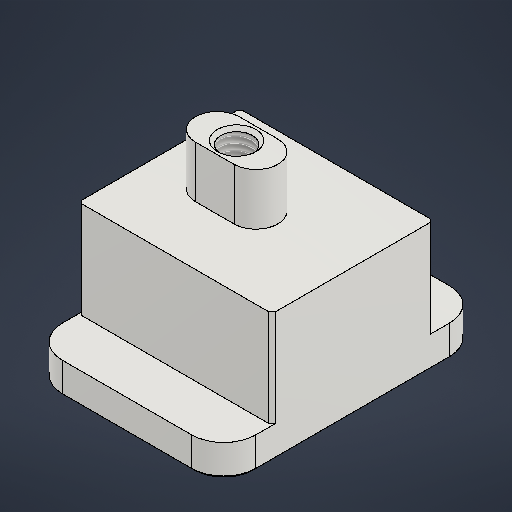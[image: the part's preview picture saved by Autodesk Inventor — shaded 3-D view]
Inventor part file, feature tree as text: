
AUTODESK INVENTOR PART (.ipt)
format: ipt  version: 2025.3 (Build 293356000, 356)  size: 249,344 bytes
history: native  units: mm
features: extrude x4, sketch x2, hole x1, fillet x1, chamfer x1
ambient origin geometry x8: Origin, YZ Plane, XZ Plane, XY Plane, X Axis, Y Axis, Z Axis, Center Point
bodies: Solid1 (feature_tree)
feature tree (9):
  sketch  "Sketch1"  dims[d0=40.0mm d1=30.0mm]
  extrude  "Extrusion1"  Depth=30.0mm
  extrude  "Extrusion2"  Depth=6.8mm
  extrude  "Extrusion5"  Depth=28.0mm
  extrude  "Extrusion6"  TaperAngle=0.0deg  [1 undecoded]
  hole  "Hole1"  [1 undecoded]
  fillet  "Fillet1"  [1 undecoded]
  chamfer  "Chamfer1"  Distance=10.0mm
  sketch  "Sketch3"  dims[d2=6.0mm d3=6.8mm d4=28.0mm d5=0.0mm d6=8.0mm d7=0.0mm d8=4.917mm d9=10.0mm d10=6.0mm d11=2.0mm d12=90.0deg d13=15.0mm d14=0.0mm d15=5.0mm d16=0.5mm d17=2.0mm d18=45.0deg d19=3.0mm d29=15.0mm d30=15.0mm d31=0.0mm d35=25.0mm d36=23.0mm d37=0.0mm]
note: 3 required parameter values undecoded (feature->parameter linkage not recoverable at this tier; creation-order binding heuristic only, values carry confidence <= 0.55)
